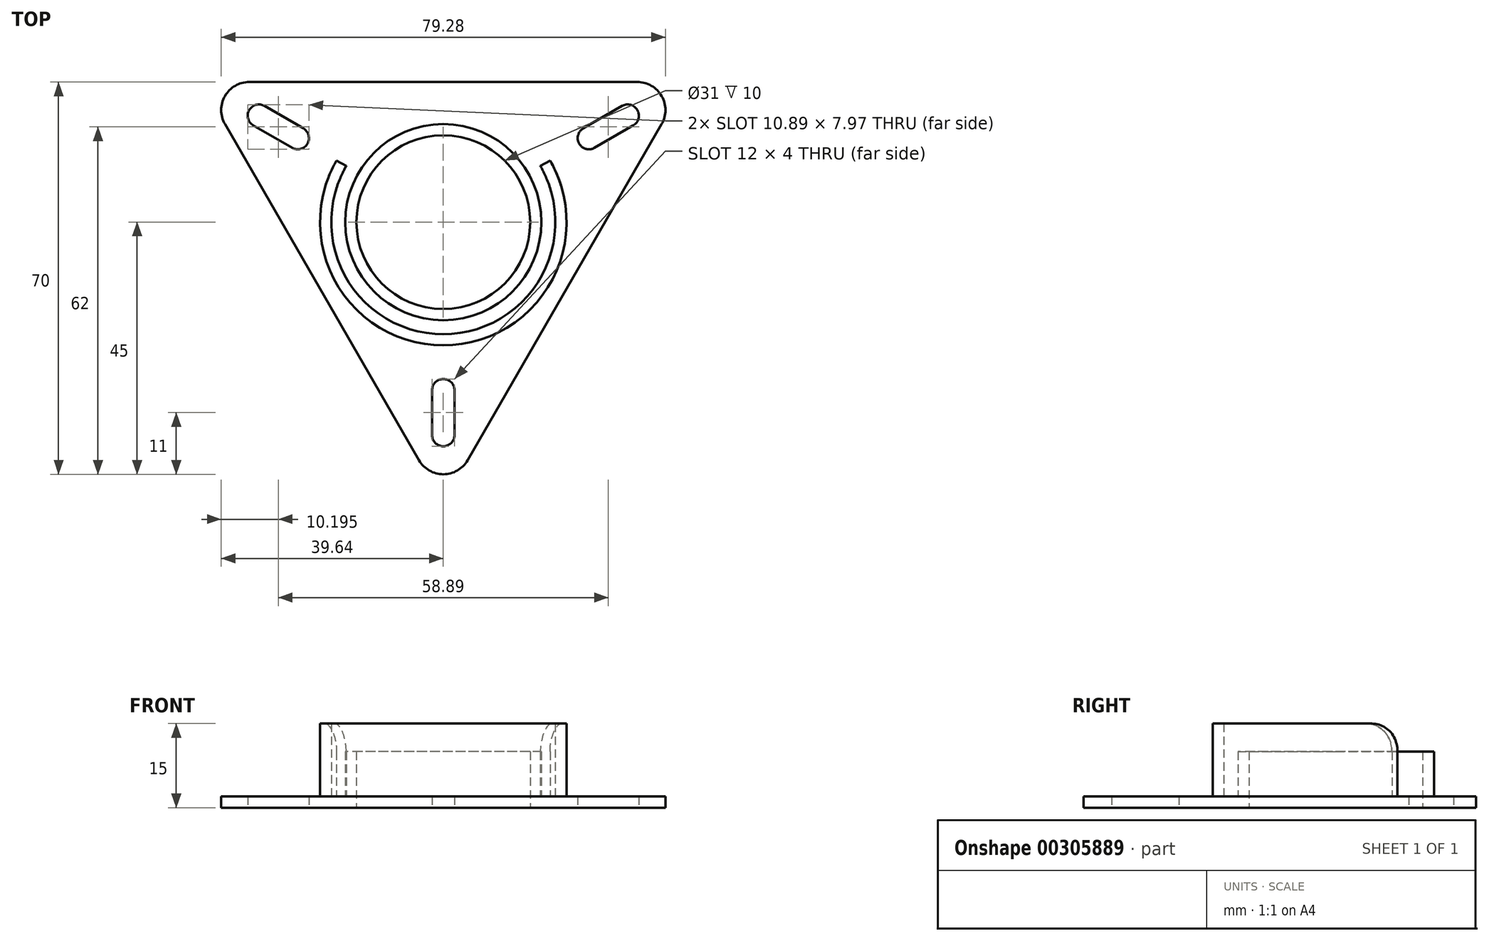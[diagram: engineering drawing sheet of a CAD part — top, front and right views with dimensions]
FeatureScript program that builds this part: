
annotation { "Feature Type Name" : "Feature", "Feature Type Description" : "" }
export const myFeature = defineFeature(function(context is Context, id is Id, definition is map)
    precondition{}
    {
        {
            var Q0;
            Q0=qCreatedBy(makeId("Top.planeOp"),FACE);
            var sketch = newSketch(context, id + "F0", { "sketchPlane" : qUnion([Q0])});
            skCircle(sketch, "E0.cCircle", {"center": v(0, 0) * mm, "radius": 25 * mm, "construction": true});
            skLineSegment(sketch, "E0.0", {"start": v(-34.64, 25) * mm, "end": v(34.64, 25) * mm});
            skLineSegment(sketch, "E0.1", {"start": v(38.97, 17.5) * mm, "end": v(4.33, -42.5) * mm});
            skLineSegment(sketch, "E0.2", {"start": v(-4.33, -42.5) * mm, "end": v(-38.97, 17.5) * mm});
            skPoint(sketch, "E0.0.midPoint", {"position": v(0, 25) * mm});
            skArc(sketch, "E1", {"start": v(-17.32, 10) * mm, "mid": v(0, -20) * mm, "end": v(17.32, 10) * mm});
            skArc(sketch, "E2", {"start": v(-19.05, 11) * mm, "mid": v(0, -22) * mm, "end": v(19.05, 11) * mm});
            skLineSegment(sketch, "E3", {"start": v(0, 0) * mm, "end": v(0, 42.42) * mm, "construction": true});
            skLineSegment(sketch, "E4", {"start": v(0, 0) * mm, "end": v(-43.3, 25) * mm, "construction": true});
            skLineSegment(sketch, "E5", {"start": v(0, 0) * mm, "end": v(43.3, 25) * mm, "construction": true});
            skLineSegment(sketch, "E6", {"start": v(0, 0) * mm, "end": v(0, -50) * mm, "construction": true});
            skPoint(sketch, "E7.visualSharp", {"position": v(-43.3, 25) * mm});
            skArc(sketch, "E7.filletArc", {"start": v(-34.64, 25) * mm, "mid": v(-38.97, 22.5) * mm, "end": v(-38.97, 17.5) * mm});
            skPoint(sketch, "E8.visualSharp", {"position": v(43.3, 25) * mm});
            skArc(sketch, "E8.filletArc", {"start": v(38.97, 17.5) * mm, "mid": v(38.97, 22.5) * mm, "end": v(34.64, 25) * mm});
            skPoint(sketch, "E9.visualSharp", {"position": v(0, -50) * mm});
            skArc(sketch, "E9.filletArc", {"start": v(-4.33, -42.5) * mm, "mid": v(0, -45) * mm, "end": v(4.33, -42.5) * mm});
            skLineSegment(sketch, "E10", {"start": v(-17.32, 10) * mm, "end": v(-19.05, 11) * mm});
            skLineSegment(sketch, "E11", {"start": v(17.32, 10) * mm, "end": v(19.05, 11) * mm});
            skLineSegment(sketch, "E12", {"start": v(-31.9, 20.73) * mm, "end": v(-24.98, 16.73) * mm});
            skLineSegment(sketch, "E13", {"start": v(-33.9, 17.27) * mm, "end": v(-26.98, 13.27) * mm});
            skArc(sketch, "E14", {"start": v(-31.9, 20.73) * mm, "mid": v(-34.64, 20) * mm, "end": v(-33.9, 17.27) * mm});
            skArc(sketch, "E15", {"start": v(-26.98, 13.27) * mm, "mid": v(-24.25, 14) * mm, "end": v(-24.98, 16.73) * mm});
            skLineSegment(sketch, "E16.1.0", {"start": v(-2, -38) * mm, "end": v(-2, -30) * mm});
            skArc(sketch, "E16.1.1", {"start": v(-2, -38) * mm, "mid": v(0, -40) * mm, "end": v(2, -38) * mm});
            skArc(sketch, "E16.1.2", {"start": v(2, -30) * mm, "mid": v(0, -28) * mm, "end": v(-2, -30) * mm});
            skLineSegment(sketch, "E16.1.3", {"start": v(2, -38) * mm, "end": v(2, -30) * mm});
            skLineSegment(sketch, "E16.2.0", {"start": v(33.9, 17.27) * mm, "end": v(26.98, 13.27) * mm});
            skArc(sketch, "E16.2.1", {"start": v(33.9, 17.27) * mm, "mid": v(34.64, 20) * mm, "end": v(31.9, 20.73) * mm});
            skArc(sketch, "E16.2.2", {"start": v(24.98, 16.73) * mm, "mid": v(24.25, 14) * mm, "end": v(26.98, 13.27) * mm});
            skLineSegment(sketch, "E16.2.3", {"start": v(31.9, 20.73) * mm, "end": v(24.98, 16.73) * mm});
            skCircle(sketch, "E17", {"center": v(0, 0) * mm, "radius": 17.5 * mm});
            skCircle(sketch, "E18", {"center": v(0, 0) * mm, "radius": 15.5 * mm});
            skSolve(sketch);
        }
        {
            var Q0;
            Q0=makeQuery(id+"F0.imprint","IMPRINT",FACE,{"disambiguationData":[TD([[makeQuery(id+"F0.imprint","IMPRINT",EDGE,{"derivedFrom":sQuery(id+"F0.wireOp",EDGE,"E0.0")}),-1.0]])]});
            extrude(context, id + "F1", {"entities" : qUnion([Q0]), "depth" : 2 * mm});
        }
        {
            var Q0;
            Q0=makeQuery(id+"F0.imprint","IMPRINT",FACE,{"disambiguationData":[TD([[makeQuery(id+"F0.imprint","IMPRINT",EDGE,{"derivedFrom":sQuery(id+"F0.wireOp",EDGE,"E1")}),-1.0]])]});
            extrude(context, id + "F2", {"entities" : qUnion([Q0]), "operationType" : NewBodyOperationType.ADD, "depth" : 15 * mm});
        }
        {
            var Q0;
            Q0=makeQuery(id+"F0.imprint","IMPRINT",FACE,{"disambiguationData":[TD([[makeQuery(id+"F0.imprint","IMPRINT",EDGE,{"derivedFrom":sQuery(id+"F0.wireOp",EDGE,"E17")}),1.0]])]});
            extrude(context, id + "F3", {"entities" : qUnion([Q0]), "operationType" : NewBodyOperationType.ADD, "depth" : 10 * mm});
        }
        {
            var Q0;
            Q0=makeQuery(id+"F2.opExtrude","CAP_EDGE",EDGE,{"disambiguationData":[OSD([sQuery(id+"F0.wireOp",EDGE,"E10")])],"isStart":false});
            var Q1;
            Q1=makeQuery(id+"F2.opExtrude","CAP_EDGE",EDGE,{"disambiguationData":[OSD([sQuery(id+"F0.wireOp",EDGE,"E11")])],"isStart":false});
            fillet(context, id + "F4", {"entities" : qUnion([Q0, Q1]), "radius" : 5 * mm, "tangentPropagation" : true, "allowEdgeOverflow" : false});
        }
    });
